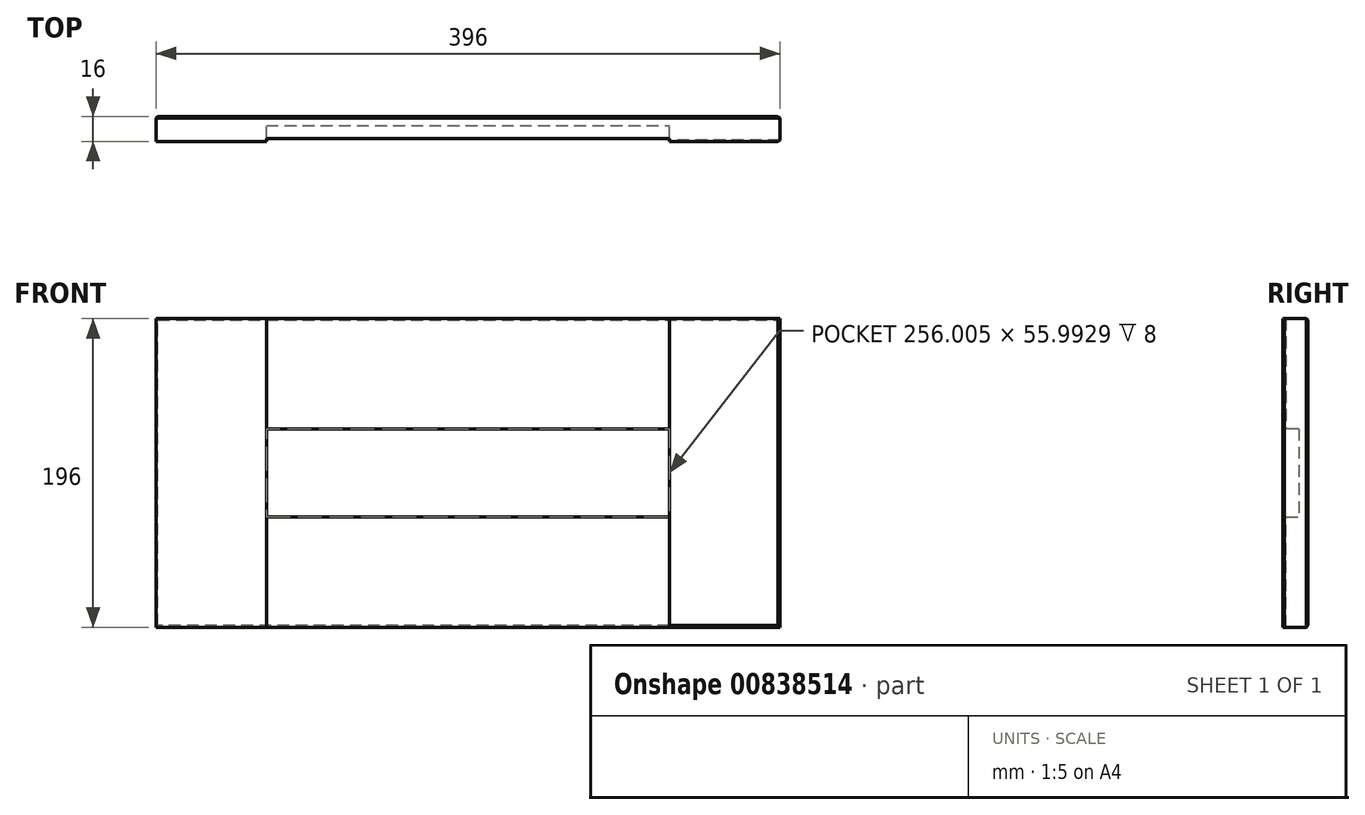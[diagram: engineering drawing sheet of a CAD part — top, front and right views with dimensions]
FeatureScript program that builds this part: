
annotation { "Feature Type Name" : "Feature", "Feature Type Description" : "" }
export const myFeature = defineFeature(function(context is Context, id is Id, definition is map)
    precondition{}
    {
        {
            var Q0;
            Q0=qCreatedBy(makeId("Front.planeOp"),FACE);
            var sketch = newSketch(context, id + "F0", { "sketchPlane" : qUnion([Q0])});
            skLineSegment(sketch, "E0.bottom", {"start": v(0, 0) * mm, "end": v(35.9, 0) * mm});
            skLineSegment(sketch, "E0.top", {"start": v(0, 30.12) * mm, "end": v(35.9, 30.12) * mm});
            skLineSegment(sketch, "E0.left", {"start": v(0, 0) * mm, "end": v(0, 30.12) * mm});
            skLineSegment(sketch, "E0.right", {"start": v(35.9, 0) * mm, "end": v(35.9, 30.12) * mm});
            skSolve(sketch);
        }
        {
            var Q0;
            Q0=makeQuery(id+"F0.imprint","IMPRINT",FACE,{"disambiguationData":[TD([[makeQuery(id+"F0.imprint","IMPRINT",EDGE,{"derivedFrom":sQuery(id+"F0.wireOp",EDGE,"E0.bottom")}),1.0]])]});
            extrude(context, id + "F1", {"entities" : qUnion([Q0]), "depth" : 16 * mm, "offsetDistance" : 25.4 * mm});
        }
        {
            var Q0;
            Q0=makeQuery(id+"F1.opExtrude","SWEPT_FACE",FACE,{"disambiguationData":[OSD([sQuery(id+"F0.wireOp",EDGE,"E0.left")])]});
            extrude(context, id + "F2", {"entities" : qUnion([Q0]), "operationType" : NewBodyOperationType.ADD, "oppositeDirection" : true, "depth" : 196 * mm, "offsetDistance" : 25 * mm});
        }
        {
            var Q0;
            {var subQ0=sQuery(id+"F0.wireOp",EDGE,"E0.bottom");Q0=makeQuery(id+"F2.boolean.opBoolean","MERGE",FACE,{"derivedFrom":[makeQuery(id+"F1.opExtrude","SWEPT_FACE",FACE,{"disambiguationData":[OSD([subQ0])]}),makeQuery(id+"F2.opExtrude","SWEPT_FACE",FACE,{"disambiguationData":[OSD([subQ0,sQuery(id+"F0.wireOp",EDGE,"E0.left")])]})]});}
            extrude(context, id + "F3", {"entities" : qUnion([Q0]), "operationType" : NewBodyOperationType.ADD, "oppositeDirection" : true, "depth" : 796 * mm, "offsetDistance" : 25 * mm});
        }
        {
            var Q0;
            {var subQ0=sQuery(id+"F0.wireOp",EDGE,"E0.left");var subQ1=sQuery(id+"F0.wireOp",EDGE,"E0.bottom");Q0=makeQuery(id+"F3.boolean.opBoolean","MERGE",FACE,{"derivedFrom":[makeQuery(id+"F2.boolean.opBoolean","MERGE",FACE,{"derivedFrom":[makeQuery(id+"F1.opExtrude","CAP_FACE",FACE,{"disambiguationData":[OSD([subQ1,sQuery(id+"F0.wireOp",EDGE,"E0.top"),subQ0,sQuery(id+"F0.wireOp",EDGE,"E0.right")])],"isStart":false}),makeQuery(id+"F2.opExtrude","SWEPT_FACE",FACE,{"disambiguationData":[OSD([subQ0]),TDD([makeQuery(id+"F1.opExtrude","CAP_EDGE",EDGE,{"disambiguationData":[OSD([subQ0])],"isStart":false})])]})]}),makeQuery(id+"F3.opExtrude","SWEPT_FACE",FACE,{"disambiguationData":[OSD([subQ1,subQ0]),TDD([makeQuery(id+"F2.boolean.opBoolean","MERGE",EDGE,{"derivedFrom":[makeQuery(id+"F1.opExtrude","CAP_EDGE",EDGE,{"disambiguationData":[OSD([subQ1])],"isStart":false}),makeQuery(id+"F2.opExtrude","SWEPT_EDGE",EDGE,{"disambiguationData":[OSD([subQ1,subQ0]),TDD([makeQuery(id+"F1.opExtrude","CAP_VERTEX",VERTEX,{"disambiguationData":[OSD([subQ1,subQ0])],"isStart":false})])]})]})])]})]});}
            var sketch = newSketch(context, id + "F4", { "sketchPlane" : qUnion([Q0])});
            skLineSegment(sketch, "E1.bottom", {"start": v(0, 796) * mm, "end": v(42.19, 796) * mm});
            skLineSegment(sketch, "E1.top", {"start": v(0, 751.57) * mm, "end": v(42.19, 751.57) * mm});
            skLineSegment(sketch, "E1.left", {"start": v(0, 796) * mm, "end": v(0, 751.57) * mm});
            skLineSegment(sketch, "E1.right", {"start": v(42.19, 796) * mm, "end": v(42.19, 751.57) * mm});
            skLineSegment(sketch, "E2.bottom", {"start": v(196, 796) * mm, "end": v(153.6, 796) * mm});
            skLineSegment(sketch, "E2.top", {"start": v(196, 746.75) * mm, "end": v(153.6, 746.75) * mm});
            skLineSegment(sketch, "E2.left", {"start": v(196, 796) * mm, "end": v(196, 746.75) * mm});
            skLineSegment(sketch, "E2.right", {"start": v(153.6, 796) * mm, "end": v(153.6, 746.75) * mm});
            skSolve(sketch);
        }
        {
            var Q0;
            Q0=makeQuery(id+"F4.imprint","IMPRINT",FACE,{"disambiguationData":[TD([[makeQuery(id+"F4.imprint","IMPRINT",EDGE,{"derivedFrom":sQuery(id+"F4.wireOp",EDGE,"E1.bottom")}),-1.0]])]});
            var Q1;
            Q1=makeQuery(id+"F4.imprint","IMPRINT",FACE,{"disambiguationData":[TD([[makeQuery(id+"F4.imprint","IMPRINT",EDGE,{"derivedFrom":sQuery(id+"F4.wireOp",EDGE,"E2.bottom")}),-1.0]])]});
            extrude(context, id + "F5", {"entities" : qUnion([Q0, Q1]), "operationType" : NewBodyOperationType.ADD, "depth" : 25 * mm, "offsetDistance" : 25 * mm});
        }
        {
            var Q0;
            {var subQ0=sQuery(id+"F0.wireOp",EDGE,"E0.left");var subQ1=sQuery(id+"F0.wireOp",EDGE,"E0.bottom");Q0=makeQuery(id+"F3.boolean.opBoolean","MERGE",FACE,{"derivedFrom":[makeQuery(id+"F2.boolean.opBoolean","MERGE",FACE,{"derivedFrom":[makeQuery(id+"F1.opExtrude","CAP_FACE",FACE,{"disambiguationData":[OSD([subQ1,sQuery(id+"F0.wireOp",EDGE,"E0.top"),subQ0,sQuery(id+"F0.wireOp",EDGE,"E0.right")])],"isStart":false}),makeQuery(id+"F2.opExtrude","SWEPT_FACE",FACE,{"disambiguationData":[OSD([subQ0]),TDD([makeQuery(id+"F1.opExtrude","CAP_EDGE",EDGE,{"disambiguationData":[OSD([subQ0])],"isStart":false})])]})]}),makeQuery(id+"F3.opExtrude","SWEPT_FACE",FACE,{"disambiguationData":[OSD([subQ1,subQ0]),TDD([makeQuery(id+"F2.boolean.opBoolean","MERGE",EDGE,{"derivedFrom":[makeQuery(id+"F1.opExtrude","CAP_EDGE",EDGE,{"disambiguationData":[OSD([subQ1])],"isStart":false}),makeQuery(id+"F2.opExtrude","SWEPT_EDGE",EDGE,{"disambiguationData":[OSD([subQ1,subQ0]),TDD([makeQuery(id+"F1.opExtrude","CAP_VERTEX",VERTEX,{"disambiguationData":[OSD([subQ1,subQ0])],"isStart":false})])]})]})])]})]});}
            var sketch = newSketch(context, id + "F6", { "sketchPlane" : qUnion([Q0])});
            skLineSegment(sketch, "E3.bottom", {"start": v(196, 0) * mm, "end": v(163.38, 0) * mm});
            skLineSegment(sketch, "E3.top", {"start": v(196, 46.55) * mm, "end": v(163.38, 46.55) * mm});
            skLineSegment(sketch, "E3.left", {"start": v(196, 0) * mm, "end": v(196, 46.55) * mm});
            skLineSegment(sketch, "E3.right", {"start": v(163.38, 0) * mm, "end": v(163.38, 46.55) * mm});
            skLineSegment(sketch, "E4.bottom", {"start": v(0, 0) * mm, "end": v(50.28, 0) * mm});
            skLineSegment(sketch, "E4.top", {"start": v(0, 44.4) * mm, "end": v(50.28, 44.4) * mm});
            skLineSegment(sketch, "E4.left", {"start": v(0, 0) * mm, "end": v(0, 44.4) * mm});
            skLineSegment(sketch, "E4.right", {"start": v(50.28, 0) * mm, "end": v(50.28, 44.4) * mm});
            skSolve(sketch);
        }
        {
            var Q0;
            Q0=makeQuery(id+"F6.imprint","IMPRINT",FACE,{"disambiguationData":[TD([[makeQuery(id+"F6.imprint","IMPRINT",EDGE,{"derivedFrom":sQuery(id+"F6.wireOp",EDGE,"E3.bottom")}),1.0]])]});
            var Q1;
            Q1=makeQuery(id+"F6.imprint","IMPRINT",FACE,{"disambiguationData":[TD([[makeQuery(id+"F6.imprint","IMPRINT",EDGE,{"derivedFrom":sQuery(id+"F6.wireOp",EDGE,"E4.bottom")}),1.0]])]});
            extrude(context, id + "F7", {"entities" : qUnion([Q0, Q1]), "operationType" : NewBodyOperationType.ADD, "depth" : 25 * mm, "offsetDistance" : 25 * mm});
        }
        {
            var Q0;
            Q0=makeQuery(id+"F7.opExtrude","SWEPT_FACE",FACE,{"disambiguationData":[OSD([sQuery(id+"F6.wireOp",EDGE,"E4.right")])]});
            extrude(context, id + "F8", {"entities" : qUnion([Q0]), "operationType" : NewBodyOperationType.ADD, "depth" : 19.72 * mm, "offsetDistance" : 25 * mm});
        }
        {
            var Q0;
            {var subQ0=sQuery(id+"F6.wireOp",EDGE,"E4.top");Q0=makeQuery(id+"F8.boolean.opBoolean","MERGE",FACE,{"derivedFrom":[makeQuery(id+"F7.opExtrude","SWEPT_FACE",FACE,{"disambiguationData":[OSD([subQ0])]}),makeQuery(id+"F8.opExtrude","SWEPT_FACE",FACE,{"disambiguationData":[OSD([subQ0,sQuery(id+"F6.wireOp",EDGE,"E4.right")])]})]});}
            extrude(context, id + "F9", {"entities" : qUnion([Q0]), "operationType" : NewBodyOperationType.ADD, "depth" : 25.6 * mm, "offsetDistance" : 25 * mm});
        }
        {
            var Q0;
            Q0=makeQuery(id+"F7.opExtrude","SWEPT_FACE",FACE,{"disambiguationData":[OSD([sQuery(id+"F6.wireOp",EDGE,"E3.right")])]});
            extrude(context, id + "F10", {"entities" : qUnion([Q0]), "operationType" : NewBodyOperationType.ADD, "depth" : 37.38 * mm, "offsetDistance" : 25 * mm});
        }
        {
            var Q0;
            {var subQ0=sQuery(id+"F6.wireOp",EDGE,"E3.top");Q0=makeQuery(id+"F10.boolean.opBoolean","MERGE",FACE,{"derivedFrom":[makeQuery(id+"F7.opExtrude","SWEPT_FACE",FACE,{"disambiguationData":[OSD([subQ0])]}),makeQuery(id+"F10.opExtrude","SWEPT_FACE",FACE,{"disambiguationData":[OSD([subQ0,sQuery(id+"F6.wireOp",EDGE,"E3.right")])]})]});}
            extrude(context, id + "F11", {"entities" : qUnion([Q0]), "operationType" : NewBodyOperationType.ADD, "depth" : 23.45 * mm, "offsetDistance" : 25 * mm});
        }
        {
            var Q0;
            Q0=makeQuery(id+"F5.opExtrude","SWEPT_FACE",FACE,{"disambiguationData":[OSD([sQuery(id+"F4.wireOp",EDGE,"E1.right")])]});
            extrude(context, id + "F12", {"entities" : qUnion([Q0]), "operationType" : NewBodyOperationType.ADD, "depth" : 27.8 * mm, "offsetDistance" : 25 * mm});
        }
        {
            var Q0;
            {var subQ0=sQuery(id+"F4.wireOp",EDGE,"E1.top");Q0=makeQuery(id+"F12.boolean.opBoolean","MERGE",FACE,{"derivedFrom":[makeQuery(id+"F5.opExtrude","SWEPT_FACE",FACE,{"disambiguationData":[OSD([subQ0])]}),makeQuery(id+"F12.opExtrude","SWEPT_FACE",FACE,{"disambiguationData":[OSD([subQ0,sQuery(id+"F4.wireOp",EDGE,"E1.right")])]})]});}
            extrude(context, id + "F13", {"entities" : qUnion([Q0]), "operationType" : NewBodyOperationType.ADD, "depth" : 25.57 * mm, "offsetDistance" : 25 * mm});
        }
        {
            var Q0;
            Q0=makeQuery(id+"F5.opExtrude","SWEPT_FACE",FACE,{"disambiguationData":[OSD([sQuery(id+"F4.wireOp",EDGE,"E2.top")])]});
            extrude(context, id + "F14", {"entities" : qUnion([Q0]), "operationType" : NewBodyOperationType.ADD, "depth" : 20.75 * mm, "offsetDistance" : 25 * mm});
        }
        {
            var Q0;
            {var subQ0=sQuery(id+"F4.wireOp",EDGE,"E2.right");Q0=makeQuery(id+"F14.boolean.opBoolean","MERGE",FACE,{"derivedFrom":[makeQuery(id+"F5.opExtrude","SWEPT_FACE",FACE,{"disambiguationData":[OSD([subQ0])]}),makeQuery(id+"F14.opExtrude","SWEPT_FACE",FACE,{"disambiguationData":[OSD([sQuery(id+"F4.wireOp",EDGE,"E2.top"),subQ0])]})]});}
            extrude(context, id + "F15", {"entities" : qUnion([Q0]), "operationType" : NewBodyOperationType.ADD, "depth" : 27.6 * mm, "offsetDistance" : 25 * mm});
        }
        {
            var Q0;
            {var subQ0=sQuery(id+"F0.wireOp",EDGE,"E0.left");var subQ1=sQuery(id+"F0.wireOp",EDGE,"E0.bottom");Q0=makeQuery(id+"F3.boolean.opBoolean","MERGE",FACE,{"derivedFrom":[makeQuery(id+"F2.boolean.opBoolean","MERGE",FACE,{"derivedFrom":[makeQuery(id+"F1.opExtrude","CAP_FACE",FACE,{"disambiguationData":[OSD([subQ1,sQuery(id+"F0.wireOp",EDGE,"E0.top"),subQ0,sQuery(id+"F0.wireOp",EDGE,"E0.right")])],"isStart":false}),makeQuery(id+"F2.opExtrude","SWEPT_FACE",FACE,{"disambiguationData":[OSD([subQ0]),TDD([makeQuery(id+"F1.opExtrude","CAP_EDGE",EDGE,{"disambiguationData":[OSD([subQ0])],"isStart":false})])]})]}),makeQuery(id+"F3.opExtrude","SWEPT_FACE",FACE,{"disambiguationData":[OSD([subQ1,subQ0]),TDD([makeQuery(id+"F2.boolean.opBoolean","MERGE",EDGE,{"derivedFrom":[makeQuery(id+"F1.opExtrude","CAP_EDGE",EDGE,{"disambiguationData":[OSD([subQ1])],"isStart":false}),makeQuery(id+"F2.opExtrude","SWEPT_EDGE",EDGE,{"disambiguationData":[OSD([subQ1,subQ0]),TDD([makeQuery(id+"F1.opExtrude","CAP_VERTEX",VERTEX,{"disambiguationData":[OSD([subQ1,subQ0])],"isStart":false})])]})]})])]})]});}
            var sketch = newSketch(context, id + "F16", { "sketchPlane" : qUnion([Q0])});
            skLineSegment(sketch, "E5.bottom", {"start": v(70, 726) * mm, "end": v(126, 726) * mm});
            skLineSegment(sketch, "E5.top", {"start": v(70, 70) * mm, "end": v(126, 70) * mm});
            skLineSegment(sketch, "E5.left", {"start": v(70, 726) * mm, "end": v(70, 70) * mm});
            skLineSegment(sketch, "E5.right", {"start": v(126, 726) * mm, "end": v(126, 70) * mm});
            skSolve(sketch);
        }
        {
            var Q0;
            Q0=makeQuery(id+"F16.imprint","IMPRINT",FACE,{"disambiguationData":[TD([[makeQuery(id+"F16.imprint","IMPRINT",EDGE,{"derivedFrom":sQuery(id+"F16.wireOp",EDGE,"E5.top")}),1.0]])]});
            extrude(context, id + "F17", {"entities" : qUnion([Q0]), "operationType" : NewBodyOperationType.REMOVE, "oppositeDirection" : true, "depth" : 10 * mm, "offsetDistance" : 25 * mm});
        }
        {
            var Q0;
            {var subQ2=sQuery(id+"F0.wireOp",EDGE,"E0.left");var subQ3=sQuery(id+"F0.wireOp",EDGE,"E0.bottom");var subQ4=makeQuery(id+"F1.opExtrude","CAP_FACE",FACE,{"disambiguationData":[OSD([subQ3,sQuery(id+"F0.wireOp",EDGE,"E0.top"),subQ2,sQuery(id+"F0.wireOp",EDGE,"E0.right")])],"isStart":false});var subQ7=makeQuery(id+"F3.opExtrude","SWEPT_FACE",FACE,{"disambiguationData":[OSD([subQ3,subQ2]),TDD([makeQuery(id+"F2.boolean.opBoolean","MERGE",EDGE,{"derivedFrom":[makeQuery(id+"F1.opExtrude","CAP_EDGE",EDGE,{"disambiguationData":[OSD([subQ3])],"isStart":false}),makeQuery(id+"F2.opExtrude","SWEPT_EDGE",EDGE,{"disambiguationData":[OSD([subQ3,subQ2]),TDD([makeQuery(id+"F1.opExtrude","CAP_VERTEX",VERTEX,{"disambiguationData":[OSD([subQ3,subQ2])],"isStart":false})])]})]})])]});var subQ8=makeQuery(id+"F2.opExtrude","SWEPT_FACE",FACE,{"disambiguationData":[OSD([subQ2]),TDD([makeQuery(id+"F1.opExtrude","CAP_EDGE",EDGE,{"disambiguationData":[OSD([subQ2])],"isStart":false})])]});Q0=makeQuery(id+"F17.boolean.opBoolean","SPLIT",FACE,{"disambiguationData":[TD([makeQuery(id+"F1.opExtrude","SWEPT_FACE",FACE,{"disambiguationData":[OSD([subQ3])]})])],"derivedFrom":makeQuery(id+"F3.boolean.opBoolean","MERGE",FACE,{"derivedFrom":[makeQuery(id+"F2.boolean.opBoolean","MERGE",FACE,{"derivedFrom":[subQ4,subQ8]}),subQ7]})});}
            var Q1;
            {var subQ2=sQuery(id+"F4.wireOp",EDGE,"E1.bottom");var subQ3=sQuery(id+"F0.wireOp",EDGE,"E0.left");var subQ4=sQuery(id+"F0.wireOp",EDGE,"E0.bottom");var subQ6=makeQuery(id+"F1.opExtrude","CAP_FACE",FACE,{"disambiguationData":[OSD([subQ4,sQuery(id+"F0.wireOp",EDGE,"E0.top"),subQ3,sQuery(id+"F0.wireOp",EDGE,"E0.right")])],"isStart":false});var subQ7=makeQuery(id+"F2.opExtrude","SWEPT_FACE",FACE,{"disambiguationData":[OSD([subQ3]),TDD([makeQuery(id+"F1.opExtrude","CAP_EDGE",EDGE,{"disambiguationData":[OSD([subQ3])],"isStart":false})])]});var subQ8=makeQuery(id+"F3.opExtrude","SWEPT_FACE",FACE,{"disambiguationData":[OSD([subQ4,subQ3]),TDD([makeQuery(id+"F2.boolean.opBoolean","MERGE",EDGE,{"derivedFrom":[makeQuery(id+"F1.opExtrude","CAP_EDGE",EDGE,{"disambiguationData":[OSD([subQ4])],"isStart":false}),makeQuery(id+"F2.opExtrude","SWEPT_EDGE",EDGE,{"disambiguationData":[OSD([subQ4,subQ3]),TDD([makeQuery(id+"F1.opExtrude","CAP_VERTEX",VERTEX,{"disambiguationData":[OSD([subQ4,subQ3])],"isStart":false})])]})]})])]});Q1=makeQuery(id+"F17.boolean.opBoolean","SPLIT",FACE,{"disambiguationData":[TD([makeQuery(id+"F5.opExtrude","SWEPT_FACE",FACE,{"disambiguationData":[OSD([subQ2])]})])],"derivedFrom":makeQuery(id+"F3.boolean.opBoolean","MERGE",FACE,{"derivedFrom":[makeQuery(id+"F2.boolean.opBoolean","MERGE",FACE,{"derivedFrom":[subQ6,subQ7]}),subQ8]})});}
            extrude(context, id + "F18", {"entities" : qUnion([Q0, Q1]), "operationType" : NewBodyOperationType.REMOVE, "oppositeDirection" : true, "depth" : 2 * mm, "offsetDistance" : 25 * mm});
        }
        {
            var Q0;
            {var subQ0=sQuery(id+"F4.wireOp",EDGE,"E1.right");var subQ1=sQuery(id+"F4.wireOp",EDGE,"E1.top");Q0=makeQuery(id+"F13.boolean.opBoolean","MERGE",FACE,{"derivedFrom":[makeQuery(id+"F12.boolean.opBoolean","MERGE",FACE,{"derivedFrom":[makeQuery(id+"F5.opExtrude","CAP_FACE",FACE,{"disambiguationData":[OSD([sQuery(id+"F4.wireOp",EDGE,"E1.bottom"),subQ1,sQuery(id+"F4.wireOp",EDGE,"E1.left"),subQ0])],"isStart":false}),makeQuery(id+"F12.opExtrude","SWEPT_FACE",FACE,{"disambiguationData":[OSD([subQ0]),TDD([makeQuery(id+"F5.opExtrude","CAP_EDGE",EDGE,{"disambiguationData":[OSD([subQ0])],"isStart":false})])]})]}),makeQuery(id+"F13.opExtrude","SWEPT_FACE",FACE,{"disambiguationData":[OSD([subQ1,subQ0]),TDD([makeQuery(id+"F12.boolean.opBoolean","MERGE",EDGE,{"derivedFrom":[makeQuery(id+"F5.opExtrude","CAP_EDGE",EDGE,{"disambiguationData":[OSD([subQ1])],"isStart":false}),makeQuery(id+"F12.opExtrude","SWEPT_EDGE",EDGE,{"disambiguationData":[OSD([subQ1,subQ0]),TDD([makeQuery(id+"F5.opExtrude","CAP_VERTEX",VERTEX,{"disambiguationData":[OSD([subQ1,subQ0])],"isStart":false})])]})]})])]})]});}
            var Q1;
            {var subQ0=sQuery(id+"F4.wireOp",EDGE,"E2.right");var subQ1=sQuery(id+"F4.wireOp",EDGE,"E2.top");Q1=makeQuery(id+"F15.boolean.opBoolean","MERGE",FACE,{"derivedFrom":[makeQuery(id+"F14.boolean.opBoolean","MERGE",FACE,{"derivedFrom":[makeQuery(id+"F5.opExtrude","CAP_FACE",FACE,{"disambiguationData":[OSD([sQuery(id+"F4.wireOp",EDGE,"E2.bottom"),subQ1,sQuery(id+"F4.wireOp",EDGE,"E2.left"),subQ0])],"isStart":false}),makeQuery(id+"F14.opExtrude","SWEPT_FACE",FACE,{"disambiguationData":[OSD([subQ1]),TDD([makeQuery(id+"F5.opExtrude","CAP_EDGE",EDGE,{"disambiguationData":[OSD([subQ1])],"isStart":false})])]})]}),makeQuery(id+"F15.opExtrude","SWEPT_FACE",FACE,{"disambiguationData":[OSD([subQ1,subQ0]),TDD([makeQuery(id+"F14.boolean.opBoolean","MERGE",EDGE,{"derivedFrom":[makeQuery(id+"F5.opExtrude","CAP_EDGE",EDGE,{"disambiguationData":[OSD([subQ0])],"isStart":false}),makeQuery(id+"F14.opExtrude","SWEPT_EDGE",EDGE,{"disambiguationData":[OSD([subQ1,subQ0]),TDD([makeQuery(id+"F5.opExtrude","CAP_VERTEX",VERTEX,{"disambiguationData":[OSD([subQ1,subQ0])],"isStart":false})])]})]})])]})]});}
            var Q2;
            {var subQ0=sQuery(id+"F6.wireOp",EDGE,"E4.right");var subQ1=sQuery(id+"F6.wireOp",EDGE,"E4.top");Q2=makeQuery(id+"F9.boolean.opBoolean","MERGE",FACE,{"derivedFrom":[makeQuery(id+"F8.boolean.opBoolean","MERGE",FACE,{"derivedFrom":[makeQuery(id+"F7.opExtrude","CAP_FACE",FACE,{"disambiguationData":[OSD([sQuery(id+"F6.wireOp",EDGE,"E4.bottom"),subQ1,sQuery(id+"F6.wireOp",EDGE,"E4.left"),subQ0])],"isStart":false}),makeQuery(id+"F8.opExtrude","SWEPT_FACE",FACE,{"disambiguationData":[OSD([subQ0]),TDD([makeQuery(id+"F7.opExtrude","CAP_EDGE",EDGE,{"disambiguationData":[OSD([subQ0])],"isStart":false})])]})]}),makeQuery(id+"F9.opExtrude","SWEPT_FACE",FACE,{"disambiguationData":[OSD([subQ1,subQ0]),TDD([makeQuery(id+"F8.boolean.opBoolean","MERGE",EDGE,{"derivedFrom":[makeQuery(id+"F7.opExtrude","CAP_EDGE",EDGE,{"disambiguationData":[OSD([subQ1])],"isStart":false}),makeQuery(id+"F8.opExtrude","SWEPT_EDGE",EDGE,{"disambiguationData":[OSD([subQ1,subQ0]),TDD([makeQuery(id+"F7.opExtrude","CAP_VERTEX",VERTEX,{"disambiguationData":[OSD([subQ1,subQ0])],"isStart":false})])]})]})])]})]});}
            var Q3;
            {var subQ0=sQuery(id+"F6.wireOp",EDGE,"E3.right");var subQ1=sQuery(id+"F6.wireOp",EDGE,"E3.top");Q3=makeQuery(id+"F11.boolean.opBoolean","MERGE",FACE,{"derivedFrom":[makeQuery(id+"F10.boolean.opBoolean","MERGE",FACE,{"derivedFrom":[makeQuery(id+"F7.opExtrude","CAP_FACE",FACE,{"disambiguationData":[OSD([sQuery(id+"F6.wireOp",EDGE,"E3.bottom"),subQ1,sQuery(id+"F6.wireOp",EDGE,"E3.left"),subQ0])],"isStart":false}),makeQuery(id+"F10.opExtrude","SWEPT_FACE",FACE,{"disambiguationData":[OSD([subQ0]),TDD([makeQuery(id+"F7.opExtrude","CAP_EDGE",EDGE,{"disambiguationData":[OSD([subQ0])],"isStart":false})])]})]}),makeQuery(id+"F11.opExtrude","SWEPT_FACE",FACE,{"disambiguationData":[OSD([subQ1,subQ0]),TDD([makeQuery(id+"F10.boolean.opBoolean","MERGE",EDGE,{"derivedFrom":[makeQuery(id+"F7.opExtrude","CAP_EDGE",EDGE,{"disambiguationData":[OSD([subQ1])],"isStart":false}),makeQuery(id+"F10.opExtrude","SWEPT_EDGE",EDGE,{"disambiguationData":[OSD([subQ1,subQ0]),TDD([makeQuery(id+"F7.opExtrude","CAP_VERTEX",VERTEX,{"disambiguationData":[OSD([subQ1,subQ0])],"isStart":false})])]})]})])]})]});}
            extrude(context, id + "F19", {"entities" : qUnion([Q0, Q1, Q2, Q3]), "operationType" : NewBodyOperationType.REMOVE, "oppositeDirection" : true, "depth" : 25 * mm, "offsetDistance" : 25 * mm});
        }
        {
            var Q0;
            {var subQ0=sQuery(id+"F4.wireOp",EDGE,"E2.left");var subQ1=sQuery(id+"F0.wireOp",EDGE,"E0.left");var subQ2=sQuery(id+"F0.wireOp",EDGE,"E0.bottom");var subQ3=sQuery(id+"F6.wireOp",EDGE,"E3.left");Q0=makeQuery(id+"F14.boolean.opBoolean","MERGE",FACE,{"derivedFrom":[makeQuery(id+"F11.boolean.opBoolean","MERGE",FACE,{"derivedFrom":[makeQuery(id+"F7.boolean.opBoolean","MERGE",FACE,{"derivedFrom":[makeQuery(id+"F5.boolean.opBoolean","MERGE",FACE,{"derivedFrom":[makeQuery(id+"F3.boolean.opBoolean","MERGE",FACE,{"derivedFrom":[makeQuery(id+"F2.opExtrude","CAP_FACE",FACE,{"disambiguationData":[OSD([subQ1])],"isStart":false}),makeQuery(id+"F3.opExtrude","SWEPT_FACE",FACE,{"disambiguationData":[OSD([subQ2,subQ1]),TDD([makeQuery(id+"F2.opExtrude","CAP_EDGE",EDGE,{"disambiguationData":[OSD([subQ2,subQ1])],"isStart":false})])]})]}),makeQuery(id+"F5.opExtrude","SWEPT_FACE",FACE,{"disambiguationData":[OSD([subQ0])]})]}),makeQuery(id+"F7.opExtrude","SWEPT_FACE",FACE,{"disambiguationData":[OSD([subQ3])]})]}),makeQuery(id+"F11.opExtrude","SWEPT_FACE",FACE,{"disambiguationData":[OSD([subQ2,subQ1,sQuery(id+"F6.wireOp",EDGE,"E3.top"),subQ3])]})]}),makeQuery(id+"F14.opExtrude","SWEPT_FACE",FACE,{"disambiguationData":[OSD([subQ2,subQ1,sQuery(id+"F4.wireOp",EDGE,"E2.top"),subQ0])]})]});}
            extrude(context, id + "F20", {"entities" : qUnion([Q0]), "operationType" : NewBodyOperationType.ADD, "depth" : 200 * mm, "offsetDistance" : 25 * mm});
        }
        {
            var Q0;
            {var subQ0=sQuery(id+"F4.wireOp",EDGE,"E2.right");var subQ1=sQuery(id+"F4.wireOp",EDGE,"E2.top");Q0=makeQuery(id+"F18.boolean.opBoolean","MERGE",FACE,{"derivedFrom":[makeQuery(id+"F15.opExtrude","CAP_FACE",FACE,{"disambiguationData":[OSD([subQ1,subQ0])],"isStart":false}),makeQuery(id+"F18.opExtrude","SWEPT_FACE",FACE,{"disambiguationData":[OSD([subQ1,subQ0])]})]});}
            var Q1;
            {var subQ0=sQuery(id+"F6.wireOp",EDGE,"E3.right");var subQ1=sQuery(id+"F6.wireOp",EDGE,"E3.top");Q1=makeQuery(id+"F18.boolean.opBoolean","MERGE",FACE,{"derivedFrom":[makeQuery(id+"F11.boolean.opBoolean","MERGE",FACE,{"derivedFrom":[makeQuery(id+"F10.opExtrude","CAP_FACE",FACE,{"disambiguationData":[OSD([subQ0])],"isStart":false}),makeQuery(id+"F11.opExtrude","SWEPT_FACE",FACE,{"disambiguationData":[OSD([subQ1,subQ0]),TDD([makeQuery(id+"F10.opExtrude","CAP_EDGE",EDGE,{"disambiguationData":[OSD([subQ1,subQ0])],"isStart":false})])]})]}),makeQuery(id+"F17.boolean.opBoolean","COPY",FACE,{"derivedFrom":makeQuery(id+"F17.opExtrude","SWEPT_FACE",FACE,{"disambiguationData":[OSD([sQuery(id+"F16.wireOp",EDGE,"E5.right")])]})}),makeQuery(id+"F18.opExtrude","SWEPT_FACE",FACE,{"disambiguationData":[OSD([subQ1,subQ0])]})]});}
            extrude(context, id + "F21", {"entities" : qUnion([Q0, Q1]), "operationType" : NewBodyOperationType.REMOVE, "oppositeDirection" : true, "depth" : 200 * mm, "offsetDistance" : 25 * mm});
        }
        {
            var Q0;
            Q0=makeQuery(id+"F17.boolean.opBoolean","COPY",FACE,{"derivedFrom":makeQuery(id+"F17.opExtrude","SWEPT_FACE",FACE,{"disambiguationData":[OSD([sQuery(id+"F16.wireOp",EDGE,"E5.bottom")])]})});
            var Q1;
            {var subQ0=sQuery(id+"F16.wireOp",EDGE,"E5.right");var subQ1=sQuery(id+"F16.wireOp",EDGE,"E5.bottom");var subQ2=sQuery(id+"F4.wireOp",EDGE,"E2.right");var subQ3=sQuery(id+"F4.wireOp",EDGE,"E2.top");var subQ4=makeQuery(id+"F17.boolean.opBoolean","COPY",EDGE,{"derivedFrom":makeQuery(id+"F17.opExtrude","SWEPT_EDGE",EDGE,{"disambiguationData":[OSD([subQ3,subQ2,subQ1,subQ0])]})});Q1=makeQuery(id+"F21.boolean.opBoolean","COPY",FACE,{"derivedFrom":makeQuery(id+"F21.opExtrude","SWEPT_FACE",FACE,{"disambiguationData":[OSD([subQ3,subQ2,subQ1,subQ0]),TDD([makeQuery(id+"F18.boolean.opBoolean","MERGE",EDGE,{"derivedFrom":[subQ4,makeQuery(id+"F18.opExtrude","SWEPT_EDGE",EDGE,{"disambiguationData":[OSD([subQ3,subQ2,subQ1,subQ0])]})]}),makeQuery(id+"F18.boolean.opBoolean","SPLIT",EDGE,{"derivedFrom":subQ4})])]})});}
            extrude(context, id + "F22", {"entities" : qUnion([Q0, Q1]), "operationType" : NewBodyOperationType.ADD, "depth" : 600 * mm, "offsetDistance" : 25 * mm});
        }
        {
            var Q0;
            {var subQ0=sQuery(id+"F4.wireOp",EDGE,"E2.bottom");var subQ1=sQuery(id+"F0.wireOp",EDGE,"E0.left");var subQ2=sQuery(id+"F0.wireOp",EDGE,"E0.bottom");var subQ3=sQuery(id+"F4.wireOp",EDGE,"E1.bottom");Q0=makeQuery(id+"F20.boolean.opBoolean","MERGE",FACE,{"derivedFrom":[makeQuery(id+"F15.boolean.opBoolean","MERGE",FACE,{"derivedFrom":[makeQuery(id+"F12.boolean.opBoolean","MERGE",FACE,{"derivedFrom":[makeQuery(id+"F5.boolean.opBoolean","MERGE",FACE,{"derivedFrom":[makeQuery(id+"F3.opExtrude","CAP_FACE",FACE,{"disambiguationData":[OSD([subQ2,subQ1])],"isStart":false}),makeQuery(id+"F5.opExtrude","SWEPT_FACE",FACE,{"disambiguationData":[OSD([subQ3])]}),makeQuery(id+"F5.opExtrude","SWEPT_FACE",FACE,{"disambiguationData":[OSD([subQ0])]})]}),makeQuery(id+"F12.opExtrude","SWEPT_FACE",FACE,{"disambiguationData":[OSD([subQ2,subQ1,subQ3,sQuery(id+"F4.wireOp",EDGE,"E1.right")])]})]}),makeQuery(id+"F15.opExtrude","SWEPT_FACE",FACE,{"disambiguationData":[OSD([subQ2,subQ1,subQ0,sQuery(id+"F4.wireOp",EDGE,"E2.right")])]})]}),makeQuery(id+"F20.opExtrude","SWEPT_FACE",FACE,{"disambiguationData":[OSD([subQ2,subQ1,subQ0,sQuery(id+"F4.wireOp",EDGE,"E2.left")])]})]});}
            extrude(context, id + "F23", {"entities" : qUnion([Q0]), "operationType" : NewBodyOperationType.REMOVE, "oppositeDirection" : true, "depth" : 600 * mm, "offsetDistance" : 25 * mm});
        }
        {
            var Q0;
            {var subQ0=sQuery(id+"F4.wireOp",EDGE,"E1.right");var subQ1=sQuery(id+"F4.wireOp",EDGE,"E1.bottom");var subQ2=sQuery(id+"F0.wireOp",EDGE,"E0.left");var subQ3=sQuery(id+"F0.wireOp",EDGE,"E0.bottom");Q0=makeQuery(id+"F23.boolean.opBoolean","COPY",EDGE,{"derivedFrom":makeQuery(id+"F23.opExtrude","CAP_EDGE",EDGE,{"disambiguationData":[OSD([subQ3,subQ2,subQ1,subQ0]),TDD([makeQuery(id+"F19.boolean.opBoolean","COPY",EDGE,{"derivedFrom":makeQuery(id+"F19.opExtrude","CAP_EDGE",EDGE,{"disambiguationData":[OSD([subQ3,subQ2,subQ1,subQ0])],"isStart":false})})])],"isStart":false})});}
            var Q1;
            {var subQ0=sQuery(id+"F0.wireOp",EDGE,"E0.left");var subQ1=sQuery(id+"F0.wireOp",EDGE,"E0.bottom");Q1=makeQuery(id+"F19.boolean.opBoolean","MERGE",EDGE,{"derivedFrom":[makeQuery(id+"F3.boolean.opBoolean","MERGE",EDGE,{"derivedFrom":[makeQuery(id+"F1.opExtrude","CAP_EDGE",EDGE,{"disambiguationData":[OSD([subQ0])],"isStart":false}),makeQuery(id+"F3.opExtrude","SWEPT_EDGE",EDGE,{"disambiguationData":[OSD([subQ1,subQ0]),TDD([makeQuery(id+"F1.opExtrude","CAP_VERTEX",VERTEX,{"disambiguationData":[OSD([subQ1,subQ0])],"isStart":false})])]})]}),makeQuery(id+"F19.opExtrude","CAP_EDGE",EDGE,{"disambiguationData":[OSD([subQ1,subQ0,sQuery(id+"F6.wireOp",EDGE,"E4.top"),sQuery(id+"F6.wireOp",EDGE,"E4.left")])],"isStart":false}),makeQuery(id+"F19.opExtrude","CAP_EDGE",EDGE,{"disambiguationData":[OSD([subQ1,subQ0,sQuery(id+"F4.wireOp",EDGE,"E1.top"),sQuery(id+"F4.wireOp",EDGE,"E1.left")])],"isStart":false})]});}
            var Q2;
            Q2=makeQuery(id+"F19.boolean.opBoolean","COPY",EDGE,{"derivedFrom":makeQuery(id+"F19.opExtrude","CAP_EDGE",EDGE,{"disambiguationData":[OSD([sQuery(id+"F0.wireOp",EDGE,"E0.bottom"),sQuery(id+"F0.wireOp",EDGE,"E0.left"),sQuery(id+"F6.wireOp",EDGE,"E4.bottom"),sQuery(id+"F6.wireOp",EDGE,"E4.right")])],"isStart":false})});
            var Q3;
            Q3=makeQuery(id+"F23.boolean.opBoolean","COPY",EDGE,{"derivedFrom":makeQuery(id+"F23.opExtrude","CAP_EDGE",EDGE,{"disambiguationData":[OSD([sQuery(id+"F0.wireOp",EDGE,"E0.bottom"),sQuery(id+"F0.wireOp",EDGE,"E0.left"),sQuery(id+"F4.wireOp",EDGE,"E2.bottom"),sQuery(id+"F4.wireOp",EDGE,"E2.left"),sQuery(id+"F4.wireOp",EDGE,"E2.right")])],"isStart":false})});
            var Q4;
            Q4=makeQuery(id+"F20.opExtrude","CAP_EDGE",EDGE,{"disambiguationData":[OSD([sQuery(id+"F0.wireOp",EDGE,"E0.bottom"),sQuery(id+"F0.wireOp",EDGE,"E0.left"),sQuery(id+"F4.wireOp",EDGE,"E2.top"),sQuery(id+"F4.wireOp",EDGE,"E2.left"),sQuery(id+"F6.wireOp",EDGE,"E3.top"),sQuery(id+"F6.wireOp",EDGE,"E3.left")])],"isStart":false});
            var Q5;
            {var subQ0=sQuery(id+"F6.wireOp",EDGE,"E3.bottom");Q5=makeQuery(id+"F20.boolean.opBoolean","MERGE",EDGE,{"derivedFrom":[makeQuery(id+"F19.boolean.opBoolean","COPY",EDGE,{"derivedFrom":makeQuery(id+"F19.opExtrude","CAP_EDGE",EDGE,{"disambiguationData":[OSD([sQuery(id+"F0.wireOp",EDGE,"E0.bottom"),sQuery(id+"F0.wireOp",EDGE,"E0.left"),subQ0,sQuery(id+"F6.wireOp",EDGE,"E3.right")])],"isStart":false})}),makeQuery(id+"F20.opExtrude","SWEPT_EDGE",EDGE,{"disambiguationData":[OSD([subQ0,sQuery(id+"F6.wireOp",EDGE,"E3.left")])]})]});}
            var Q6;
            {var subQ0=sQuery(id+"F0.wireOp",EDGE,"E0.left");var subQ1=sQuery(id+"F0.wireOp",EDGE,"E0.bottom");Q6=makeQuery(id+"F20.boolean.opBoolean","MERGE",FACE,{"derivedFrom":[makeQuery(id+"F3.boolean.opBoolean","MERGE",FACE,{"derivedFrom":[makeQuery(id+"F2.boolean.opBoolean","MERGE",FACE,{"derivedFrom":[makeQuery(id+"F1.opExtrude","CAP_FACE",FACE,{"disambiguationData":[OSD([subQ1,sQuery(id+"F0.wireOp",EDGE,"E0.top"),subQ0,sQuery(id+"F0.wireOp",EDGE,"E0.right")])],"isStart":true}),makeQuery(id+"F2.opExtrude","SWEPT_FACE",FACE,{"disambiguationData":[OSD([subQ0]),TDD([makeQuery(id+"F1.opExtrude","CAP_EDGE",EDGE,{"disambiguationData":[OSD([subQ0])],"isStart":true})])]})]}),makeQuery(id+"F3.opExtrude","SWEPT_FACE",FACE,{"disambiguationData":[OSD([subQ1,subQ0]),TDD([makeQuery(id+"F2.boolean.opBoolean","MERGE",EDGE,{"derivedFrom":[makeQuery(id+"F1.opExtrude","CAP_EDGE",EDGE,{"disambiguationData":[OSD([subQ1])],"isStart":true}),makeQuery(id+"F2.opExtrude","SWEPT_EDGE",EDGE,{"disambiguationData":[OSD([subQ1,subQ0]),TDD([makeQuery(id+"F1.opExtrude","CAP_VERTEX",VERTEX,{"disambiguationData":[OSD([subQ1,subQ0])],"isStart":true})])]})]})])]})]}),makeQuery(id+"F20.opExtrude","SWEPT_FACE",FACE,{"disambiguationData":[OSD([subQ1,subQ0])]})]});}
            chamfer(context, id + "F24", {"entities" : qUnion([Q0, Q1, Q2, Q3, Q4, Q5, Q6]), "width" : 1 * mm, "tangentPropagation" : true});
        }
    });
